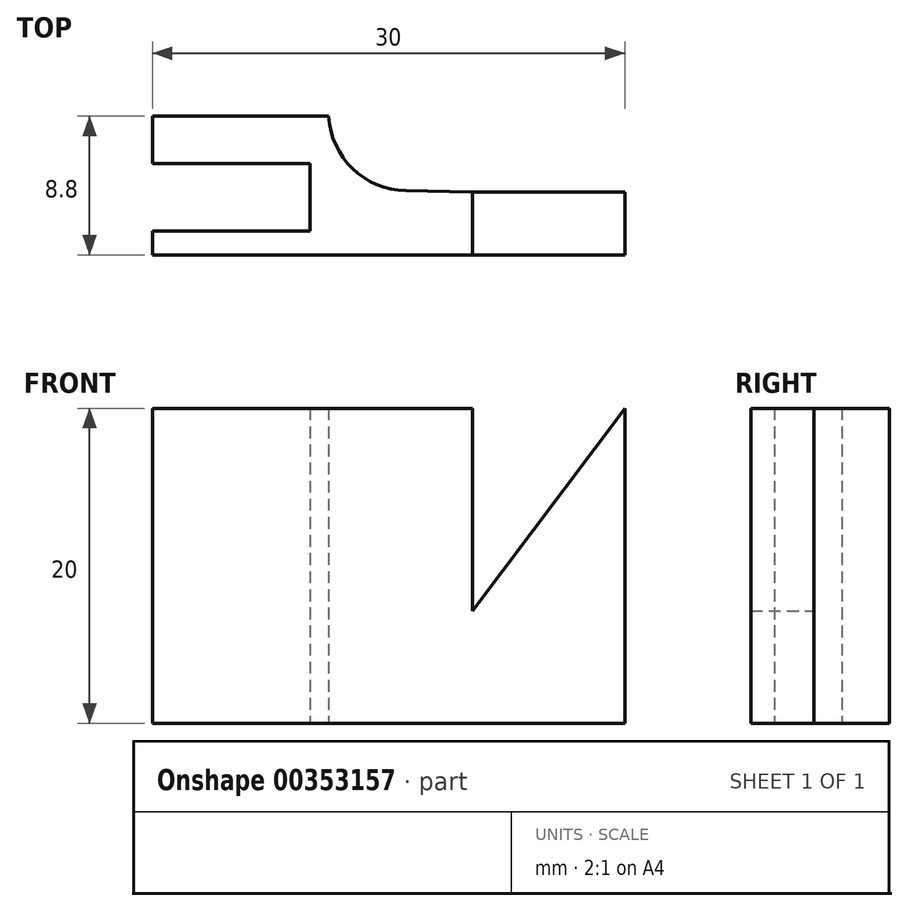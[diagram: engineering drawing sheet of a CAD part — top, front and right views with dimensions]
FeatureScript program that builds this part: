
annotation { "Feature Type Name" : "Feature", "Feature Type Description" : "" }
export const myFeature = defineFeature(function(context is Context, id is Id, definition is map)
    precondition{}
    {
        {
            var Q0;
            Q0=qCreatedBy(makeId("Top.planeOp"),FACE);
            var sketch = newSketch(context, id + "F0", { "sketchPlane" : qUnion([Q0])});
            skLineSegment(sketch, "E0", {"start": v(0, 0) * mm, "end": v(0, 2.99) * mm});
            skLineSegment(sketch, "E1", {"start": v(-30, 8.8) * mm, "end": v(-30, 5.8) * mm});
            skLineSegment(sketch, "E2", {"start": v(-30, 5.8) * mm, "end": v(-20, 5.8) * mm});
            skLineSegment(sketch, "E3", {"start": v(-9.73, 4) * mm, "end": v(0, 4) * mm});
            skLineSegment(sketch, "E4", {"start": v(0, 4) * mm, "end": v(0, 2.99) * mm});
            skLineSegment(sketch, "E5", {"start": v(0, 2.99) * mm, "end": v(0, 1.5) * mm});
            skLineSegment(sketch, "E6", {"start": v(-20, 1.5) * mm, "end": v(-20, 5.8) * mm});
            skLineSegment(sketch, "E7", {"start": v(-20, 1.5) * mm, "end": v(-30, 1.5) * mm});
            skLineSegment(sketch, "E8", {"start": v(-30, 1.5) * mm, "end": v(-30, 0) * mm});
            skLineSegment(sketch, "E9", {"start": v(-30, 0) * mm, "end": v(0, 0) * mm});
            skLineSegment(sketch, "E10", {"start": v(-30, 8.8) * mm, "end": v(-18.8, 8.8) * mm});
            skLineSegment(sketch, "E11", {"start": v(-18.8, 8.8) * mm, "end": v(-18.8, 4.17) * mm});
            skLineSegment(sketch, "E12", {"start": v(-18.8, 4.17) * mm, "end": v(-9.73, 4) * mm});
            skSolve(sketch);
        }
        {
            var Q0;
            Q0 = qSketchRegion(id + "F0", true);
            extrude(context, id + "F1", {"entities" : qUnion([Q0]), "depth" : 20 * mm});
        }
        {
            var Q0;
            Q0=makeQuery(id+"F1.opExtrude","SWEPT_EDGE",EDGE,{"disambiguationData":[OSD([sQuery(id+"F0.wireOp",EDGE,"E3"),sQuery(id+"F0.wireOp",EDGE,"E12")])]});
            var Q1;
            Q1=makeQuery(id+"F1.opExtrude","SWEPT_EDGE",EDGE,{"disambiguationData":[OSD([sQuery(id+"F0.wireOp",EDGE,"E11"),sQuery(id+"F0.wireOp",EDGE,"E12")])]});
            fillet(context, id + "F2", {"entities" : qUnion([Q0, Q1]), "radius" : 5 * mm, "tangentPropagation" : true, "allowEdgeOverflow" : false});
        }
        {
            var Q0;
            Q0=makeQuery(id+"F1.opExtrude","SWEPT_FACE",FACE,{"disambiguationData":[OSD([sQuery(id+"F0.wireOp",EDGE,"E3")])]});
            var sketch = newSketch(context, id + "F3", { "sketchPlane" : qUnion([Q0])});
            skLineSegment(sketch, "E13", {"start": v(0, 0) * mm, "end": v(15.05, 20) * mm});
            skLineSegment(sketch, "E14", {"start": v(15.05, 20) * mm, "end": v(15.05, 0) * mm});
            skLineSegment(sketch, "E15", {"start": v(15.05, 0) * mm, "end": v(0, 20) * mm});
            skCircle(sketch, "E16", {"center": v(7.53, 10) * mm, "radius": 1.75 * mm});
            skSolve(sketch);
        }
        {
            var Q0;
            {var subQ0=sQuery(id+"F3.wireOp",EDGE,"E15");var subQ1=sQuery(id+"F3.wireOp",EDGE,"E13");var subQ2=makeQuery(id+"F3.imprint","INTERSECT",VERTEX,{"derivedFrom":[subQ1,subQ0]});Q0=makeQuery(id+"F3.imprint","IMPRINT",FACE,{"disambiguationData":[TD([[makeQuery(id+"F3.imprint","IMPRINT",EDGE,{"disambiguationData":[TD([[subQ2,-1.0]])],"derivedFrom":subQ1}),1.0]])]});}
            var Q1;
            {var subQ0=sQuery(id+"F3.wireOp",EDGE,"E16");var subQ1=sQuery(id+"F3.wireOp",EDGE,"E13");var subQ2=makeQuery(id+"F3.imprint","INTERSECT",VERTEX,{"disambiguationData":[OD(0.0)],"derivedFrom":[subQ1,subQ0]});Q1=makeQuery(id+"F3.imprint","IMPRINT",FACE,{"disambiguationData":[TD([[makeQuery(id+"F3.imprint","IMPRINT",EDGE,{"disambiguationData":[TD([[subQ2,-1.0]])],"derivedFrom":subQ1}),1.0]])]});}
            var Q2;
            {var subQ0=sQuery(id+"F3.wireOp",EDGE,"E16");var subQ1=sQuery(id+"F3.wireOp",EDGE,"E13");var subQ2=makeQuery(id+"F3.imprint","INTERSECT",VERTEX,{"disambiguationData":[OD(0.0)],"derivedFrom":[subQ1,subQ0]});Q2=makeQuery(id+"F3.imprint","IMPRINT",FACE,{"disambiguationData":[TD([[makeQuery(id+"F3.imprint","IMPRINT",EDGE,{"disambiguationData":[TD([[subQ2,-1.0]])],"derivedFrom":subQ1}),-1.0]])]});}
            var Q3;
            {var subQ0=sQuery(id+"F3.wireOp",EDGE,"E15");var subQ1=sQuery(id+"F3.wireOp",EDGE,"E13");var subQ2=makeQuery(id+"F3.imprint","INTERSECT",VERTEX,{"derivedFrom":[subQ1,subQ0]});Q3=makeQuery(id+"F3.imprint","IMPRINT",FACE,{"disambiguationData":[TD([[makeQuery(id+"F3.imprint","IMPRINT",EDGE,{"disambiguationData":[TD([[subQ2,-1.0]])],"derivedFrom":subQ1}),-1.0]])]});}
            extrude(context, id + "F4", {"entities" : qUnion([Q0, Q1, Q2, Q3]), "operationType" : NewBodyOperationType.REMOVE, "oppositeDirection" : true, "depth" : 25 * mm});
        }
    });
